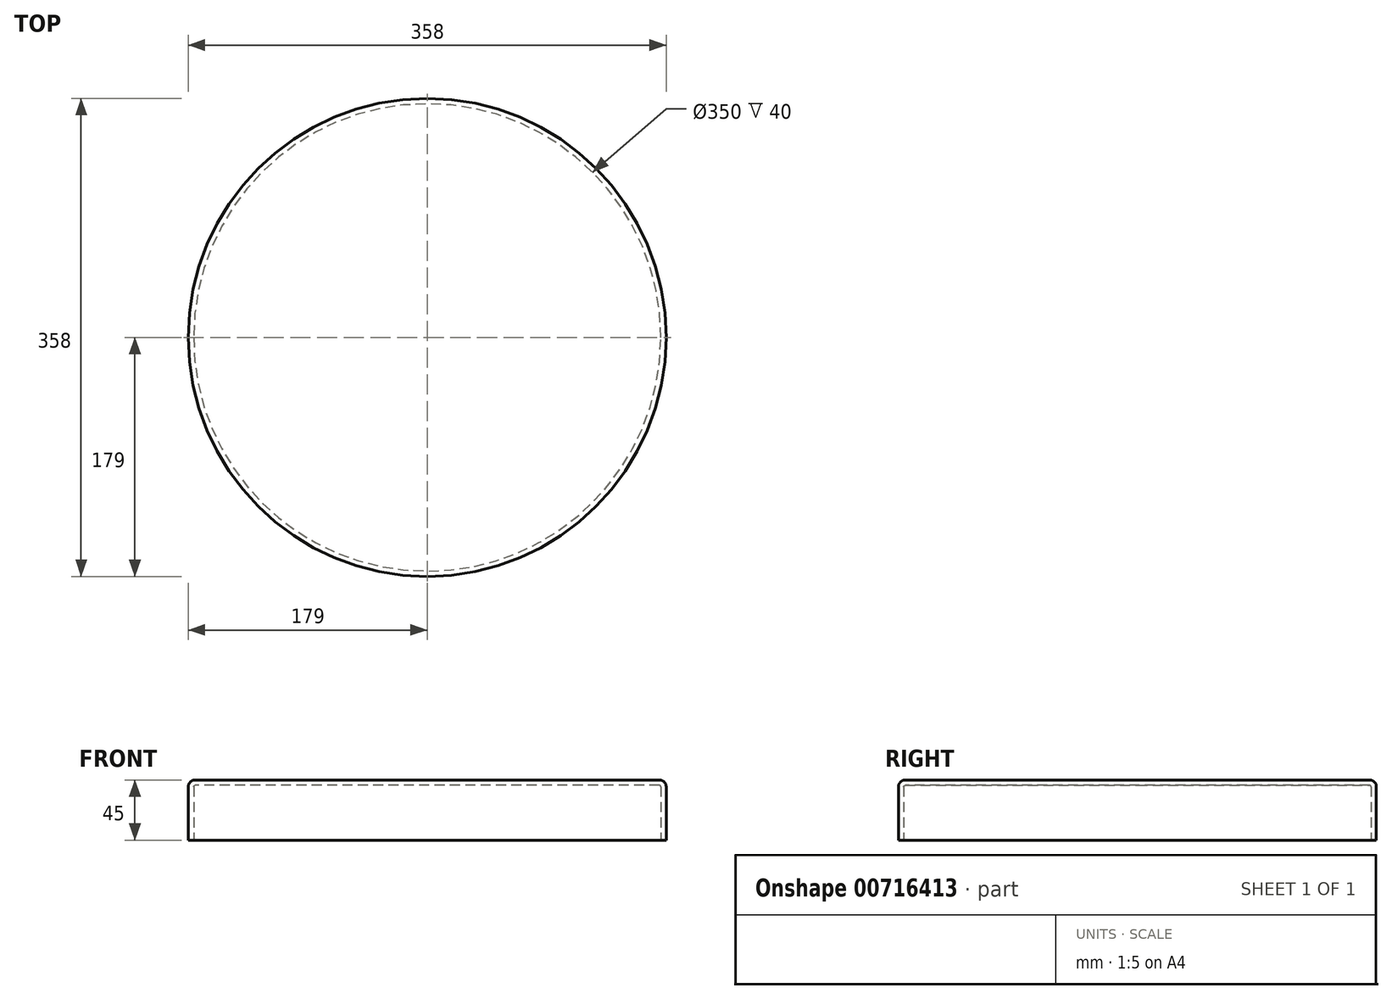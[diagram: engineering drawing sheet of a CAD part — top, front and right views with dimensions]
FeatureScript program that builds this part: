
annotation { "Feature Type Name" : "Feature", "Feature Type Description" : "" }
export const myFeature = defineFeature(function(context is Context, id is Id, definition is map)
    precondition{}
    {
        {
            var Q0;
            Q0=qCreatedBy(makeId("Top.planeOp"),FACE);
            var sketch = newSketch(context, id + "F0", { "sketchPlane" : qUnion([Q0])});
            skCircle(sketch, "E0", {"center": v(0, 0) * mm, "radius": 179 * mm});
            skSolve(sketch);
        }
        {
            var Q0;
            Q0 = qSketchRegion(id + "F0", true);
            extrude(context, id + "F1", {"entities" : qUnion([Q0]), "depth" : 45 * mm, "offsetDistance" : 25 * mm});
        }
        {
            var Q0;
            Q0=makeQuery(id+"F1.opExtrude","CAP_EDGE",EDGE,{"disambiguationData":[OSD([sQuery(id+"F0.wireOp",EDGE,"E0")])],"isStart":false});
            fillet(context, id + "F2", {"entities" : qUnion([Q0]), "radius" : 5 * mm, "tangentPropagation" : true, "allowEdgeOverflow" : false});
        }
        {
            var Q0;
            Q0=makeQuery(id+"F1.opExtrude","CAP_FACE",FACE,{"disambiguationData":[OSD([sQuery(id+"F0.wireOp",EDGE,"E0")])],"isStart":true});
            shell(context, id + "F3", {"entities" : qUnion([Q0]), "thickness" : 4 * mm});
        }
    });
